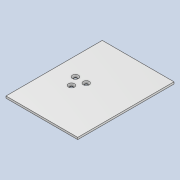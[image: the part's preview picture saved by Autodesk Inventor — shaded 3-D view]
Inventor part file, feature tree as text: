
AUTODESK INVENTOR PART (.ipt)
format: ipt  version: 2022 (Build 260153000, 153)  size: 103,424 bytes
history: native  units: in
note: dims shown in document units (in); Inventor stores cm internally (conversion verified against a paired STEP export)
features: other x1, sketch x1, extrude x1, hole x1
ambient origin geometry x8: Origin, YZ Plane, XZ Plane, XY Plane, X Axis, Y Axis, Z Axis, Center Point
bodies: Body1 (feature_tree)
feature tree (4):
  other  "ソリッド1"
  sketch  "スケッチ1"
  extrude  "押し出し1"  Depth=7.874in
  hole  "穴1"  [1 undecoded]
note: 1 required parameter value undecoded (feature->parameter linkage not recoverable at this tier; creation-order binding heuristic only, values carry confidence <= 0.55)
